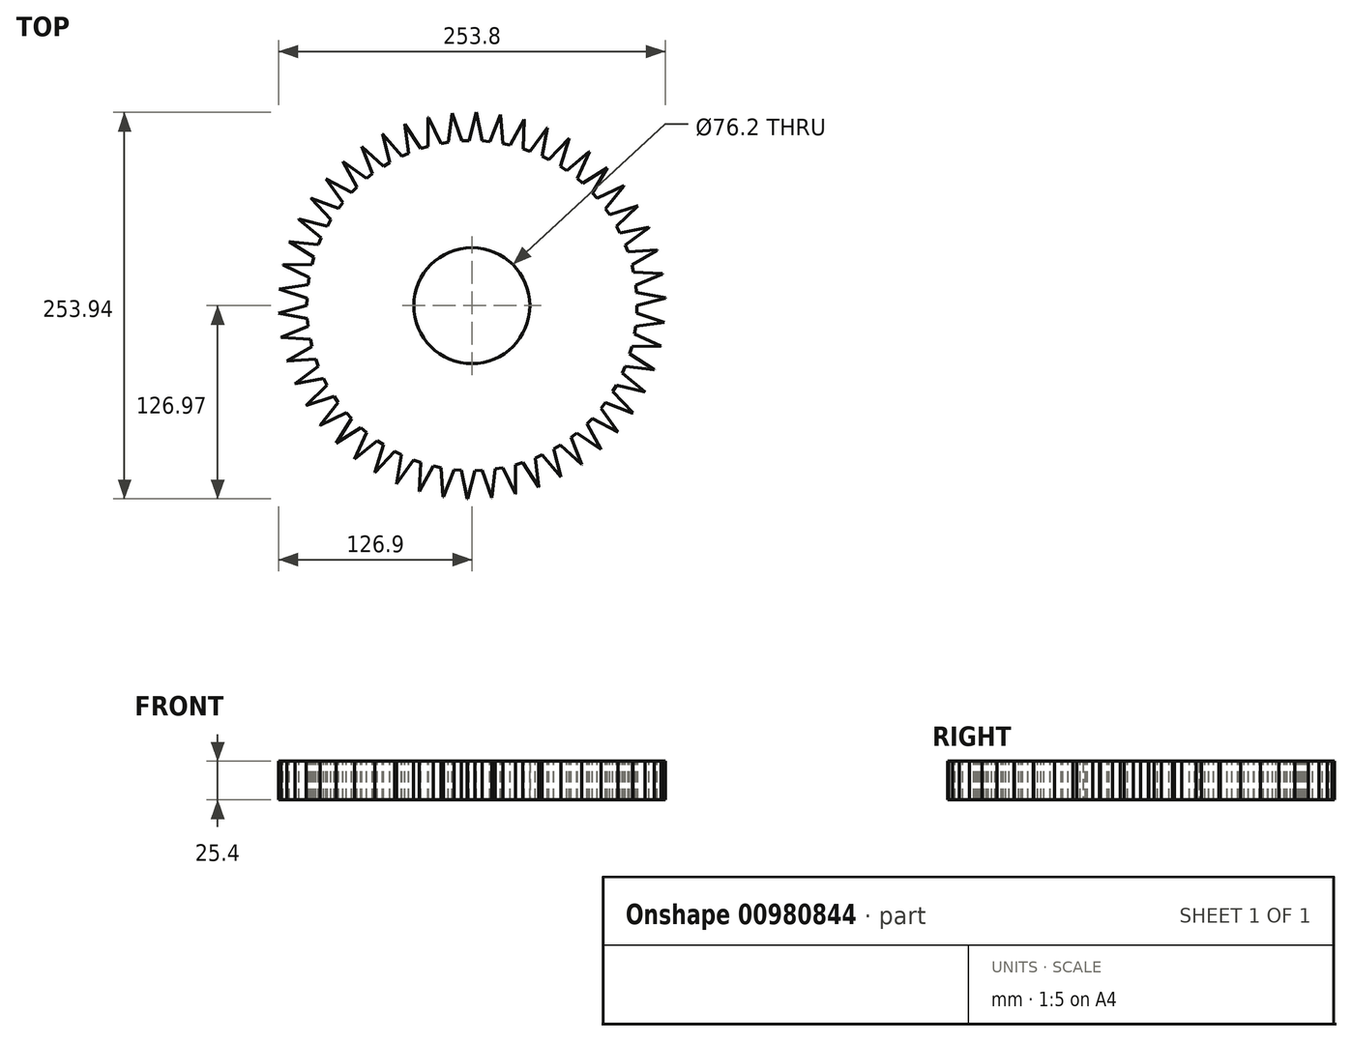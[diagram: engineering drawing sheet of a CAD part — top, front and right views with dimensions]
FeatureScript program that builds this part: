
annotation { "Feature Type Name" : "Feature", "Feature Type Description" : "" }
export const myFeature = defineFeature(function(context is Context, id is Id, definition is map)
    precondition{}
    {
        {
            var Q0;
            Q0=qCreatedBy(makeId("Top.planeOp"),FACE);
            var sketch = newSketch(context, id + "F0", { "sketchPlane" : qUnion([Q0])});
            skCircle(sketch, "E0", {"center": v(0, 0) * mm, "radius": 127 * mm});
            skCircle(sketch, "E1", {"center": v(0, 0) * mm, "radius": 38.1 * mm});
            skSolve(sketch);
        }
        {
            var Q0;
            Q0 = qSketchRegion(id + "F0", true);
            extrude(context, id + "F1", {"entities" : qUnion([Q0]), "depth" : 25.4 * mm, "offsetDistance" : 25.4 * mm});
        }
        {
            var Q0;
            Q0=makeQuery(id+"F1.opExtrude","CAP_FACE",FACE,{"disambiguationData":[OSD([sQuery(id+"F0.wireOp",EDGE,"E0"),sQuery(id+"F0.wireOp",EDGE,"E1")])],"isStart":false});
            var sketch = newSketch(context, id + "F2", { "sketchPlane" : qUnion([Q0])});
            skLineSegment(sketch, "E2", {"start": v(-43.95, 119.15) * mm, "end": v(-33.43, 103.14) * mm});
            skLineSegment(sketch, "E3", {"start": v(-28.74, 104.55) * mm, "end": v(-28.74, 123.7) * mm});
            skLineSegment(sketch, "E4", {"start": v(-28.74, 104.55) * mm, "end": v(-33.43, 103.14) * mm});
            skSolve(sketch);
        }
        {
            var Q0;
            Q0=qCreatedBy(makeId("Front.planeOp"),FACE);
            var sketch = newSketch(context, id + "F3", { "sketchPlane" : qUnion([Q0])});
            skLineSegment(sketch, "E5", {"start": v(0, 0) * mm, "end": v(0, -64.68) * mm, "construction": true});
            skSolve(sketch);
        }
        {
            var Q0;
            {var subQ0=sQuery(id+"F2.wireOp",EDGE,"E2");Q0=makeQuery(id+"F2.imprint","IMPRINT",FACE,{"disambiguationData":[TD([[makeQuery(id+"F2.imprint","IMPRINT",EDGE,{"derivedFrom":subQ0}),1.0]])]});}
            extrude(context, id + "F4", {"entities" : qUnion([Q0]), "operationType" : NewBodyOperationType.REMOVE, "endBound" : BoundingType.UP_TO_NEXT, "oppositeDirection" : true, "depth" : 25.4 * mm, "offsetDistance" : 25.4 * mm});
        }
        {
            var Q0;
            Q0=makeQuery(id+"F4.boolean.opBoolean","COPY",FACE,{"derivedFrom":makeQuery(id+"F4.opExtrude","SWEPT_FACE",FACE,{"disambiguationData":[OSD([sQuery(id+"F2.wireOp",EDGE,"E2")])]})});
            var Q1;
            Q1=makeQuery(id+"F4.boolean.opBoolean","COPY",FACE,{"derivedFrom":makeQuery(id+"F4.opExtrude","SWEPT_FACE",FACE,{"disambiguationData":[OSD([sQuery(id+"F2.wireOp",EDGE,"E4")])]})});
            var Q2;
            Q2=makeQuery(id+"F4.boolean.opBoolean","COPY",FACE,{"derivedFrom":makeQuery(id+"F4.opExtrude","SWEPT_FACE",FACE,{"disambiguationData":[OSD([sQuery(id+"F2.wireOp",EDGE,"E3")])]})});
            var Q3;
            Q3=sQuery(id+"F3.wireOp",EDGE,"E5");
            circularPattern(context, id + "F5", {"patternType" : PatternType.FACE, "faces" : qUnion([Q0, Q1, Q2]), "axis" : qUnion([Q3]), "angle" : 360 * degree, "instanceCount" : 50, "equalSpace" : true});
        }
    });
